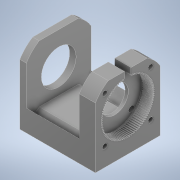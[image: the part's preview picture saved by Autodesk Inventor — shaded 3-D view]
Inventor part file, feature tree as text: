
AUTODESK INVENTOR PART (.ipt)
format: ipt  version: 2022 (Build 260153000, 153)  size: 699,904 bytes
history: mixed  units: in
note: dims shown in document units (in); Inventor stores cm internally (conversion verified against a paired STEP export)
features: extrude x10, sketch x10, plane x1, other x1, imported_body x1
ambient origin geometry x8: Origin, YZ Plane, XZ Plane, XY Plane, X Axis, Y Axis, Z Axis, Center Point
bodies: Solid1 (imported_parasolid)
feature tree (23):
  extrude  "Extrusion1"  Depth=0.3937in TaperAngle=0.0deg
  plane  "Work Plane1"
  extrude  "Extrusion2"  Depth=0.9843in TaperAngle=0.0deg
  extrude  "Extrusion5"  TaperAngle=0.0deg  [1 undecoded]
  extrude  "Extrusion6"  Depth=0.5906in TaperAngle=0.0deg
  extrude  "Extrusion7"  Depth=0.0984in
  extrude  "Extrusion8"  Depth=0.3937in TaperAngle=0.0deg
  extrude  "Extrusion9"  Depth=0.2362in TaperAngle=0.0deg
  extrude  "Extrusion10"  Depth=0.2362in
  extrude  "Extrusion11"  Depth=0.0197in
  extrude  "Extrusion12"  [1 undecoded]
  sketch  "Sketch2"  dims[d1=0.3937in d2=0.0in d3=0.3937in d4=0.0in]
  sketch  "Sketch3"  dims[d9=0.2756in d10=0.9843in d11=0.0in]
  sketch  "Sketch6"  dims[d12=0.7874in d13=0.0in d14=0.0in]
  sketch  "Sketch7"  dims[d15=0.5906in d16=0.0in d17=1.1811in d18=0.0in]
  sketch  "Sketch8"  dims[d19=0.5906in d20=0.0in d25=0.0984in]
  sketch  "Sketch9"  dims[d26=0.0984in d27=0.3937in d28=0.0in]
  sketch  "Sketch10"  dims[d29=1.2697in d30=0.2362in d31=0.0in]
  sketch  "Sketch11"  dims[d32=0.1181in d33=0.2362in]
  sketch  "Sketch12"  dims[d34=0.7087in d35=0.0in d7=0.0197in]
  sketch  "Sketch13"  dims[d8=0.0344in]
  other  "96_Teeth_Gear.STEP"
  imported_body  NMx_Import_Brep_tag  [imported B-rep: ~421 faces, bbox_mm=[70.0, 68.027756, 60.0]]
note: 2 required parameter values undecoded (feature->parameter linkage not recoverable at this tier; creation-order binding heuristic only, values carry confidence <= 0.55)
